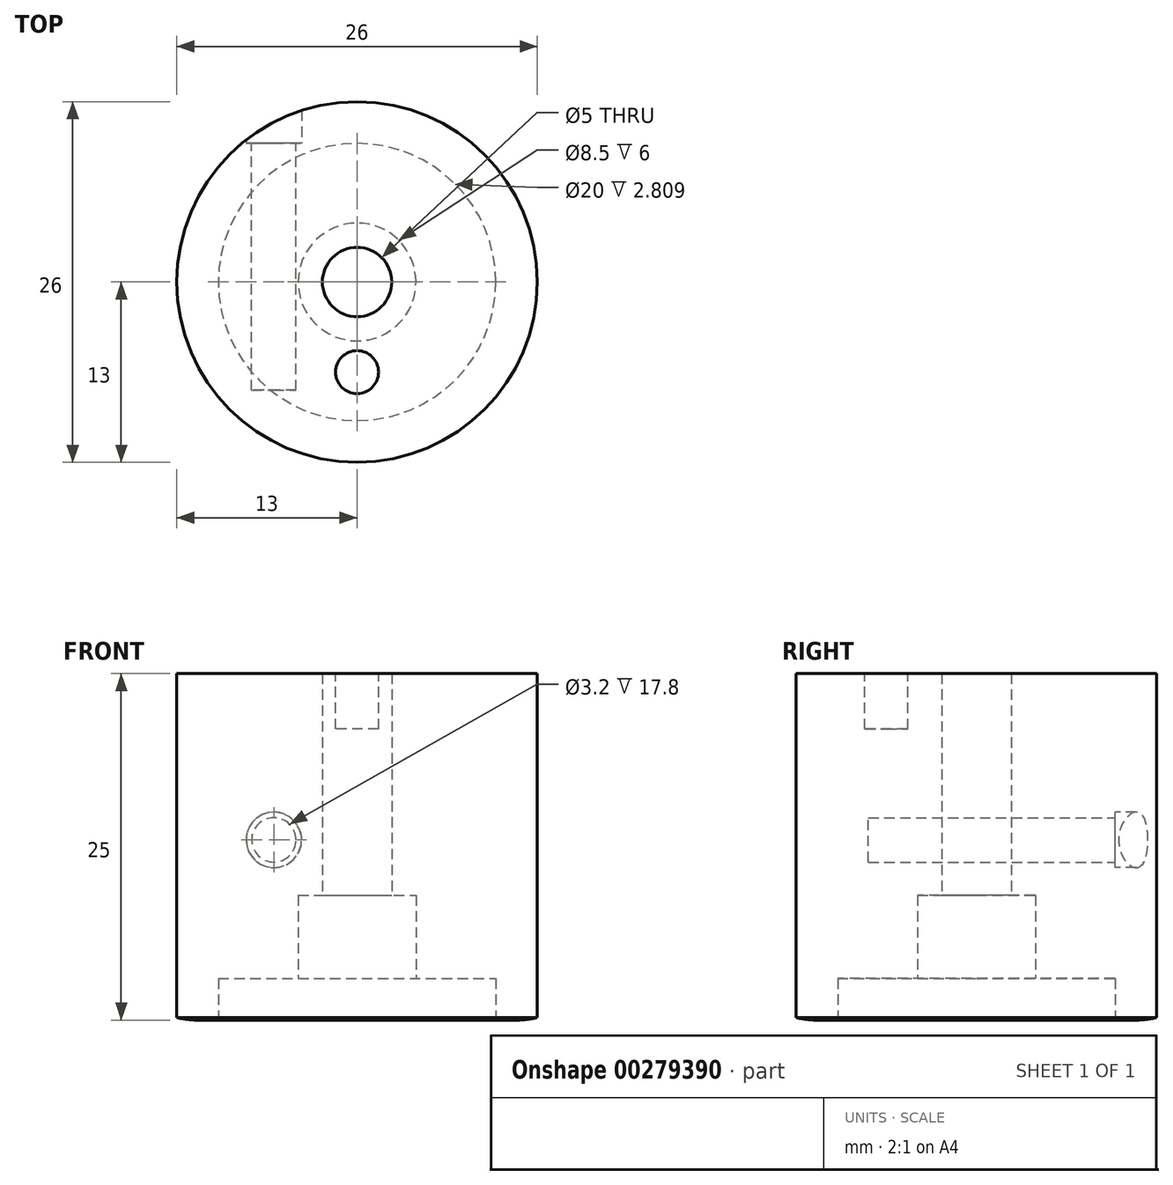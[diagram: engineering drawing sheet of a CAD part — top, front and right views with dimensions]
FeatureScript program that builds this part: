
annotation { "Feature Type Name" : "Feature", "Feature Type Description" : "" }
export const myFeature = defineFeature(function(context is Context, id is Id, definition is map)
    precondition{}
    {
        {
            var Q0;
            Q0=qCreatedBy(makeId("Front.planeOp"),FACE);
            var sketch = newSketch(context, id + "F0", { "sketchPlane" : qUnion([Q0])});
            skLineSegment(sketch, "E0", {"start": v(0, 0) * mm, "end": v(11.5, 0) * mm, "construction": true});
            skLineSegment(sketch, "E1", {"start": v(11.5, 0) * mm, "end": v(11.5, 6) * mm, "construction": true});
            skArc(sketch, "E2", {"start": v(10, 0.2) * mm, "mid": v(11.5, 0) * mm, "end": v(13, 0.2) * mm});
            skLineSegment(sketch, "E3", {"start": v(0, 0) * mm, "end": v(0, 25) * mm, "construction": true});
            skLineSegment(sketch, "E4", {"start": v(0, 25) * mm, "end": v(2.5, 25) * mm, "construction": true});
            skLineSegment(sketch, "E5", {"start": v(2.5, 25) * mm, "end": v(13, 25) * mm});
            skLineSegment(sketch, "E6", {"start": v(13, 25) * mm, "end": v(13, 0.2) * mm});
            skLineSegment(sketch, "E7", {"start": v(0, 0) * mm, "end": v(10, 0) * mm, "construction": true});
            skLineSegment(sketch, "E8", {"start": v(10, 0.2) * mm, "end": v(10, 3) * mm});
            skLineSegment(sketch, "E9", {"start": v(10, 3) * mm, "end": v(4.25, 3) * mm});
            skLineSegment(sketch, "E10", {"start": v(4.25, 3) * mm, "end": v(4.25, 9) * mm});
            skLineSegment(sketch, "E11", {"start": v(4.25, 9) * mm, "end": v(2.5, 9) * mm});
            skLineSegment(sketch, "E12", {"start": v(2.5, 9) * mm, "end": v(2.5, 25) * mm});
            skLineSegment(sketch, "E13", {"start": v(0, 0) * mm, "end": v(-6, 0) * mm, "construction": true});
            skLineSegment(sketch, "E14", {"start": v(-6, 0) * mm, "end": v(-6, 13) * mm, "construction": true});
            skCircle(sketch, "E15", {"center": v(-6, 13) * mm, "radius": 1.6 * mm});
            skCircle(sketch, "E16", {"center": v(-6, 13) * mm, "radius": 2 * mm});
            skSolve(sketch);
        }
        {
            var Q0;
            Q0=makeQuery(id+"F0.imprint","IMPRINT",FACE,{"disambiguationData":[TD([[makeQuery(id+"F0.imprint","IMPRINT",EDGE,{"derivedFrom":sQuery(id+"F0.wireOp",EDGE,"E2")}),1.0]])]});
            var Q1;
            Q1=sQuery(id+"F0.wireOp",EDGE,"E3");
            revolve(context, id + "F1", {"entities" : qUnion([Q0]), "axis" : qUnion([Q1]), "revolveType" : RevolveType.FULL});
        }
        {
            var Q0;
            Q0=qCreatedBy(makeId("Top.planeOp"),FACE);
            var sketch = newSketch(context, id + "F2", { "sketchPlane" : qUnion([Q0])});
            skLineSegment(sketch, "E17", {"start": v(0, 0) * mm, "end": v(0, -6.5) * mm, "construction": true});
            skCircle(sketch, "E18", {"center": v(0, -6.5) * mm, "radius": 1.55 * mm});
            skSolve(sketch);
        }
        {
            var Q0;
            Q0=qCreatedBy(makeId("Top.planeOp"),FACE);
            cPlane(context, id + "F3", {"entities" : qUnion([Q0]), "cplaneType" : CPlaneType.OFFSET, "offset" : 25 * mm, "width" : 150 * mm, "height" : 150 * mm});
        }
        {
            var Q0;
            Q0=qCreatedBy(id+"F3.planeOp",FACE);
            var sketch = newSketch(context, id + "F4", { "sketchPlane" : qUnion([Q0])});
            skCircle(sketch, "E19.0", {"center": v(0, -6.5) * mm, "radius": 1.55 * mm});
            skSolve(sketch);
        }
        {
            var Q0;
            Q0=makeQuery(id+"F4.imprint","IMPRINT",FACE,{"disambiguationData":[TD([[makeQuery(id+"F4.imprint","IMPRINT",EDGE,{"derivedFrom":sQuery(id+"F4.wireOp",EDGE,"E19.0")}),1.0]])]});
            var Q1;
            Q1=sQuery(id+"F4.wireOp",EDGE,"E19.0");
            extrude(context, id + "F5", {"entities" : qUnion([Q0]), "operationType" : NewBodyOperationType.REMOVE, "surfaceEntities" : qUnion([Q1]), "oppositeDirection" : true, "depth" : 4 * mm});
        }
        {
            var Q0;
            Q0=qCreatedBy(makeId("Front.planeOp"),FACE);
            cPlane(context, id + "F6", {"entities" : qUnion([Q0]), "cplaneType" : CPlaneType.OFFSET, "offset" : 13 * mm, "oppositeDirection" : true, "width" : 150 * mm, "height" : 150 * mm});
        }
        {
            var Q0;
            Q0=qCreatedBy(id+"F6.planeOp",FACE);
            var sketch = newSketch(context, id + "F7", { "sketchPlane" : qUnion([Q0])});
            skCircle(sketch, "E20.0", {"center": v(-6, 13) * mm, "radius": 1.6 * mm});
            skSolve(sketch);
        }
        {
            var Q0;
            Q0=makeQuery(id+"F7.imprint","IMPRINT",FACE,{"disambiguationData":[TD([[makeQuery(id+"F7.imprint","IMPRINT",EDGE,{"derivedFrom":sQuery(id+"F7.wireOp",EDGE,"E20.0")}),1.0]])]});
            extrude(context, id + "F8", {"entities" : qUnion([Q0]), "operationType" : NewBodyOperationType.REMOVE, "depth" : 20.8 * mm});
        }
        {
            var Q0;
            Q0=qCreatedBy(makeId("Front.planeOp"),FACE);
            cPlane(context, id + "F9", {"entities" : qUnion([Q0]), "cplaneType" : CPlaneType.OFFSET, "offset" : 10 * mm, "oppositeDirection" : true, "width" : 150 * mm, "height" : 150 * mm});
        }
        {
            var Q0;
            Q0=qCreatedBy(id+"F9.planeOp",FACE);
            var sketch = newSketch(context, id + "F10", { "sketchPlane" : qUnion([Q0])});
            skCircle(sketch, "E21.0", {"center": v(-6, 13) * mm, "radius": 2 * mm});
            skSolve(sketch);
        }
        {
            var Q0;
            Q0 = qSketchRegion(id + "F10", true);
            extrude(context, id + "F11", {"entities" : qUnion([Q0]), "operationType" : NewBodyOperationType.REMOVE, "oppositeDirection" : true, "depth" : 3 * mm});
        }
    });
